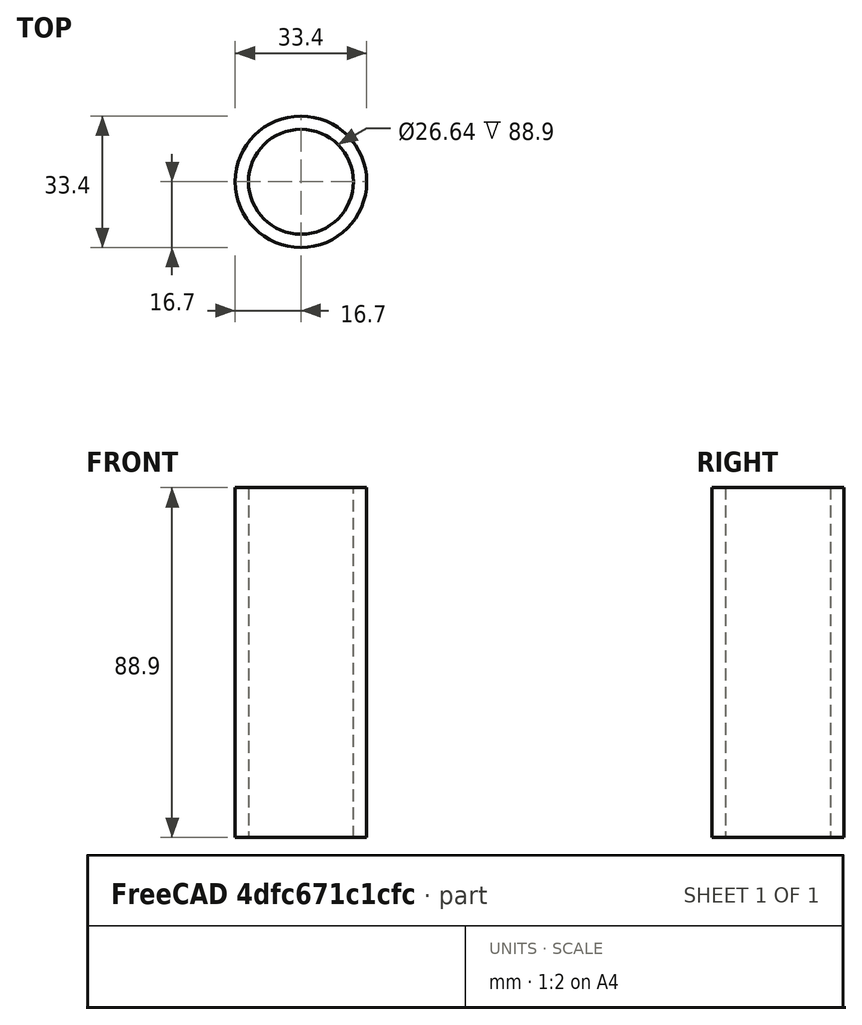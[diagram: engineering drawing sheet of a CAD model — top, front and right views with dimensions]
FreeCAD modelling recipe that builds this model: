
FCSTD DOCUMENT  (FreeCAD 0.20R29177 +426 (Git))
Label: PipeNipple
License: All rights reserved
LicenseURL: http://en.wikipedia.org/wiki/All_rights_reserved
objects: PartDesign::CoordinateSystem×2, Sketcher::SketchObject×1, PartDesign::Pad×1, PartDesign::Body×1
note: 6 computed .brp shape members not serialized (recipe doc carries the construction recipe); baked Part::Feature solids carry a one-line shape summary decoded from their .brp

FEATURE [Sketcher::SketchObject] Sketch
  FullyConstrained = true
  MapMode = 5
  Support = -> [XY_Plane]
  sketch-geometry (2):
    g0: Circle CenterX=0 CenterY=0 CenterZ=0 NormalX=0 NormalY=0 NormalZ=1 AngleXU=0 Radius=13.3223
    g1: Circle CenterX=0 CenterY=0 CenterZ=0 NormalX=0 NormalY=0 NormalZ=1 AngleXU=0 Radius=16.7005
  constraints (4):
    c: Coincident(g0,g-1)
    c: Coincident(g1,g0)
    c: Diameter(g1) = 33.401
    c: Diameter(g0) = 26.6446
FEATURE [PartDesign::Pad] Pad
  Direction = (0,0,1)
  Length = 88.9
  Length2 = 10
  Profile = -> Sketch
  ReferenceAxis = -> Sketch [N_Axis]
  Type = 0
FEATURE [PartDesign::CoordinateSystem] LCS_root
  AttacherType = Attacher::AttachEngine3D
  MapMode = 2
  Support = -> [XY_Plane]
FEATURE [PartDesign::CoordinateSystem] LCS_end
  AttacherType = Attacher::AttachEngine3D
  AttachmentOffset = pos=(0,0,88.9) rot=(0,0,1;0rad)
  MapMode = 2
  Placement = pos=(0,0,88.9) rot=(0,0,1;0rad)
  Support = -> [LCS_root]
  expr: .AttachmentOffset.Base.z = <<Pad>>.Length
FEATURE [PartDesign::Body] Body
  Group = -> [Sketch,Pad,LCS_root,LCS_end]
  Origin = -> Origin
  Tip = -> Pad
